# Revit family: Flushometer SLOAN
name_source: partatom
category: Plumbing Fixtures
revit_build: Autodesk Revit 2018 (Build: 20170223_1515(x64)
units: mm (PartAtom-declared; Revit-internal decimal feet)

## family parameters
Cut with Voids When Loaded = No
Host = Face
OmniClass Number = 23.45.05.21.11.21
OmniClass Title = Urinals
Part Type = Normal
Room Calculation Point = No
Round Connector Dimension = Use Diameter
Shared = No

## types (3) — shared parameters
ADA Compliant = Yes
CW Connection = Yes
Connection Diameter = 1 "
Default Elevation = 48 "
Faceplate Material = ZAMAK Chrome plated
Fixture Type = Urinal
HW Connection = No
Height = 7 "
Manufacturer = SLOAN
Material = ZAMAK Chrome plated
Operating Pressure = 0.7 to 5.5 Bar
Price = Prices may vary. Please consult Manufacturer Representative for most up-to-date price list.
Supply C/L to finished wall  (MIN, MAX) = 3.5" to 4.5"
URL = https://www.sloan.com
Valve Inlet Size = G 1/2"
Valve Outlet Size = G 1/2"
Vent Connection = No
Waste Connection = No
Width = 5 "

## per-type parameters (varying)
| type | Flush Cycle | SKU |
| SGV-7910 | 1.0 Lpf/0.25 gpf | 33440003 |
| SGV-7905 | 0.5 Lpf/0.125 gpf | 33440002 |
| SGV-7915 | 1.5 Lpf/0.40 gpf | 33440004 |

note: column(s) folded — value = type name in every type: Model

## geometry (parser evidence)
native form markers: Sweep x2
no freeform markers — native parametric forms only
